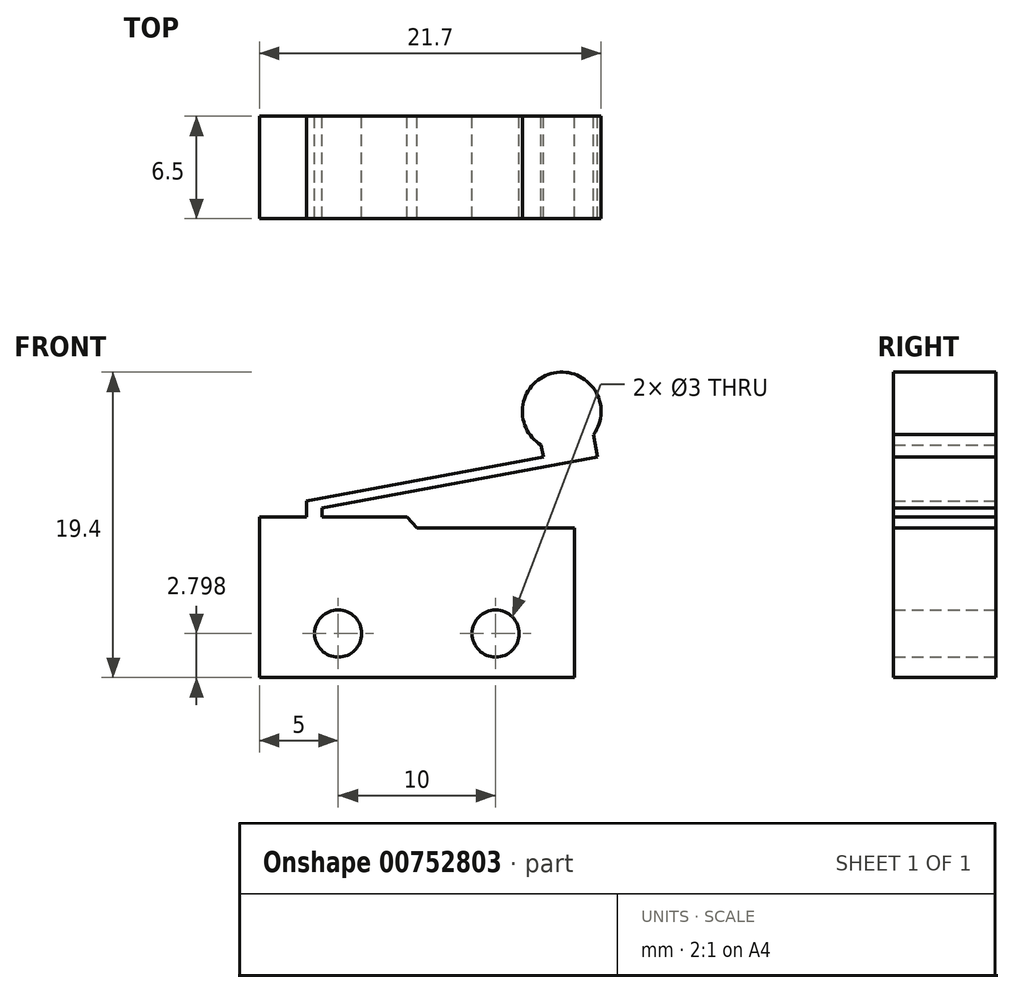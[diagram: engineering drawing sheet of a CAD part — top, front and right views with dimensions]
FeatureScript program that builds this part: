
annotation { "Feature Type Name" : "Feature", "Feature Type Description" : "" }
export const myFeature = defineFeature(function(context is Context, id is Id, definition is map)
    precondition{}
    {
        {
            var Q0;
            Q0=qCreatedBy(makeId("Front.planeOp"),FACE);
            var sketch = newSketch(context, id + "F0", { "sketchPlane" : qUnion([Q0])});
            skLineSegment(sketch, "E0", {"start": v(-8.34, -5.26) * mm, "end": v(11.66, -5.26) * mm});
            skLineSegment(sketch, "E1", {"start": v(11.66, -5.26) * mm, "end": v(11.66, 4.24) * mm});
            skLineSegment(sketch, "E2", {"start": v(11.66, 4.24) * mm, "end": v(1.66, 4.24) * mm});
            skLineSegment(sketch, "E3", {"start": v(1.66, 4.24) * mm, "end": v(1.05, 4.94) * mm});
            skLineSegment(sketch, "E4", {"start": v(1.05, 4.94) * mm, "end": v(-8.34, 4.94) * mm});
            skLineSegment(sketch, "E5", {"start": v(-8.34, 4.94) * mm, "end": v(-8.34, -5.26) * mm});
            skLineSegment(sketch, "E6", {"start": v(-5.34, 4.94) * mm, "end": v(-5.34, 5.96) * mm});
            skLineSegment(sketch, "E7", {"start": v(-5.34, 5.96) * mm, "end": v(9.7, 8.74) * mm});
            skLineSegment(sketch, "E8", {"start": v(9.7, 8.74) * mm, "end": v(9.56, 9.5) * mm});
            skArc(sketch, "E9", {"start": v(12.89, 10.17) * mm, "mid": v(10.37, 14.09) * mm, "end": v(9.56, 9.5) * mm});
            skLineSegment(sketch, "E10", {"start": v(12.89, 10.17) * mm, "end": v(13.15, 8.76) * mm});
            skLineSegment(sketch, "E11", {"start": v(13.15, 8.76) * mm, "end": v(-4.37, 5.52) * mm});
            skLineSegment(sketch, "E12", {"start": v(-4.37, 5.52) * mm, "end": v(-4.37, 4.94) * mm});
            skCircle(sketch, "E13", {"center": v(-3.34, -2.46) * mm, "radius": 1.5 * mm});
            skCircle(sketch, "E14", {"center": v(6.66, -2.46) * mm, "radius": 1.5 * mm});
            skSolve(sketch);
        }
        {
            var Q0;
            Q0=makeQuery(id+"F0.imprint","IMPRINT",FACE,{"disambiguationData":[TD([[makeQuery(id+"F0.imprint","IMPRINT",EDGE,{"derivedFrom":sQuery(id+"F0.wireOp",EDGE,"E0")}),1.0]])]});
            var Q1;
            Q1 = qSketchRegion(id + "F0", true);
            extrude(context, id + "F1", {"entities" : qUnion([Q0, Q1]), "depth" : 6.5 * mm, "offsetDistance" : 25 * mm});
        }
    });
